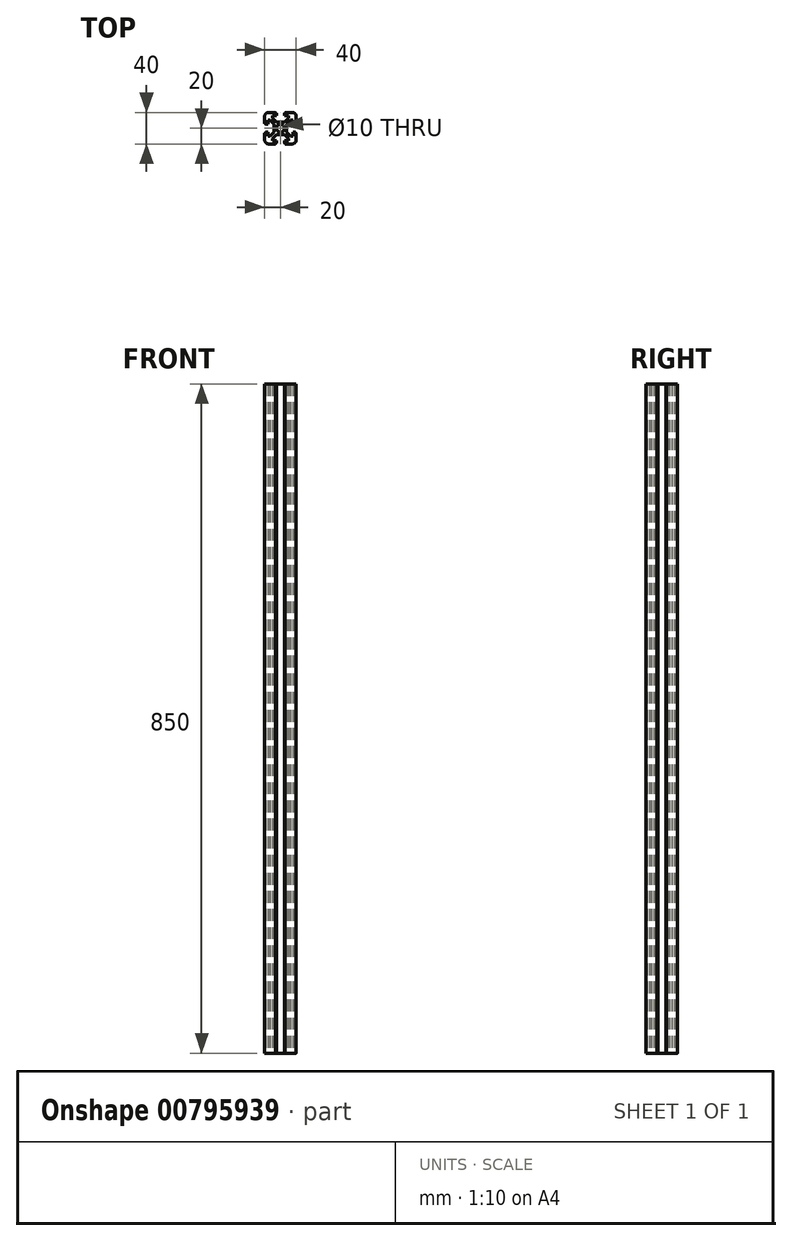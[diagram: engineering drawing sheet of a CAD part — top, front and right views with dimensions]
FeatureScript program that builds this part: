
annotation { "Feature Type Name" : "Feature", "Feature Type Description" : "" }
export const myFeature = defineFeature(function(context is Context, id is Id, definition is map)
    precondition{}
    {
        {
            var Q0;
            Q0=qCreatedBy(makeId("Top.planeOp"),FACE);
            var sketch = newSketch(context, id + "F0", { "sketchPlane" : qUnion([Q0])});
            skLineSegment(sketch, "E0", {"start": v(22.87, 22.87) * mm, "end": v(0, 0) * mm, "construction": true});
            skLineSegment(sketch, "E1", {"start": v(8, 0) * mm, "end": v(8, 5) * mm});
            skLineSegment(sketch, "E2", {"start": v(8, 5) * mm, "end": v(13, 10) * mm});
            skLineSegment(sketch, "E3", {"start": v(13, 10) * mm, "end": v(16, 10) * mm});
            skLineSegment(sketch, "E4", {"start": v(16, 10) * mm, "end": v(16, 5) * mm});
            skLineSegment(sketch, "E5", {"start": v(16, 5) * mm, "end": v(19, 5) * mm});
            skLineSegment(sketch, "E6", {"start": v(19, 5) * mm, "end": v(19, 6) * mm});
            skLineSegment(sketch, "E7", {"start": v(19, 6) * mm, "end": v(20, 6) * mm});
            skLineSegment(sketch, "E8", {"start": v(20, 6) * mm, "end": v(20, 15) * mm});
            skArc(sketch, "E9", {"start": v(20, 15) * mm, "mid": v(19.62, 16.91) * mm, "end": v(18.54, 18.54) * mm});
            skPoint(sketch, "E9.third.point", {"position": v(18.54, 18.54) * mm});
            skLineSegment(sketch, "E10.MirrorCS", {"start": v(6, 19) * mm, "end": v(6, 20) * mm});
            skLineSegment(sketch, "E11.MirrorCS", {"start": v(5, 19) * mm, "end": v(6, 19) * mm});
            skLineSegment(sketch, "E12.MirrorCS", {"start": v(6, 20) * mm, "end": v(15, 20) * mm});
            skLineSegment(sketch, "E13.MirrorCS", {"start": v(5, 16) * mm, "end": v(5, 19) * mm});
            skLineSegment(sketch, "E14.MirrorCS", {"start": v(10, 16) * mm, "end": v(5, 16) * mm});
            skLineSegment(sketch, "E15.MirrorCS", {"start": v(10, 13) * mm, "end": v(10, 16) * mm});
            skLineSegment(sketch, "E16.MirrorCS", {"start": v(5, 8) * mm, "end": v(10, 13) * mm});
            skLineSegment(sketch, "E17.MirrorCS", {"start": v(0, 8) * mm, "end": v(5, 8) * mm});
            skArc(sketch, "E18.MirrorCS", {"start": v(15, 20) * mm, "mid": v(16.91, 19.62) * mm, "end": v(18.54, 18.54) * mm});
            skLineSegment(sketch, "E19.1.0", {"start": v(-13, 10) * mm, "end": v(-16, 10) * mm});
            skLineSegment(sketch, "E19.1.1", {"start": v(-16, 10) * mm, "end": v(-16, 5) * mm});
            skLineSegment(sketch, "E19.1.2", {"start": v(-8, 5) * mm, "end": v(-13, 10) * mm});
            skPoint(sketch, "E19.1.3", {"position": v(-18.54, 18.54) * mm});
            skLineSegment(sketch, "E19.1.4", {"start": v(-8, 0) * mm, "end": v(-8, 5) * mm});
            skLineSegment(sketch, "E19.1.5", {"start": v(-16, 5) * mm, "end": v(-19, 5) * mm});
            skArc(sketch, "E19.1.6", {"start": v(-20, 15) * mm, "mid": v(-19.62, 16.91) * mm, "end": v(-18.54, 18.54) * mm});
            skLineSegment(sketch, "E19.1.7", {"start": v(-20, 6) * mm, "end": v(-20, 15) * mm});
            skArc(sketch, "E19.1.8", {"start": v(-15, 20) * mm, "mid": v(-16.91, 19.62) * mm, "end": v(-18.54, 18.54) * mm});
            skLineSegment(sketch, "E19.1.9", {"start": v(-6, 20) * mm, "end": v(-15, 20) * mm});
            skLineSegment(sketch, "E19.1.10", {"start": v(-5, 16) * mm, "end": v(-5, 19) * mm});
            skLineSegment(sketch, "E19.1.11", {"start": v(-10, 16) * mm, "end": v(-5, 16) * mm});
            skLineSegment(sketch, "E19.1.12", {"start": v(-5, 8) * mm, "end": v(-10, 13) * mm});
            skLineSegment(sketch, "E19.1.13", {"start": v(-10, 13) * mm, "end": v(-10, 16) * mm});
            skLineSegment(sketch, "E19.1.14", {"start": v(0, 8) * mm, "end": v(-5, 8) * mm});
            skPoint(sketch, "E19.1.15", {"position": v(-18.54, 18.54) * mm});
            skLineSegment(sketch, "E19.1.16", {"start": v(-19, 5) * mm, "end": v(-19, 6) * mm});
            skLineSegment(sketch, "E19.1.17", {"start": v(-19, 6) * mm, "end": v(-20, 6) * mm});
            skLineSegment(sketch, "E19.1.18", {"start": v(-6, 19) * mm, "end": v(-6, 20) * mm});
            skLineSegment(sketch, "E19.1.19", {"start": v(-5, 19) * mm, "end": v(-6, 19) * mm});
            skLineSegment(sketch, "E19.2.0", {"start": v(-10, -13) * mm, "end": v(-10, -16) * mm});
            skLineSegment(sketch, "E19.2.1", {"start": v(-10, -16) * mm, "end": v(-5, -16) * mm});
            skLineSegment(sketch, "E19.2.2", {"start": v(-5, -8) * mm, "end": v(-10, -13) * mm});
            skPoint(sketch, "E19.2.3", {"position": v(-18.54, -18.54) * mm});
            skLineSegment(sketch, "E19.2.4", {"start": v(0, -8) * mm, "end": v(-5, -8) * mm});
            skLineSegment(sketch, "E19.2.5", {"start": v(-5, -16) * mm, "end": v(-5, -19) * mm});
            skArc(sketch, "E19.2.6", {"start": v(-15, -20) * mm, "mid": v(-16.91, -19.62) * mm, "end": v(-18.54, -18.54) * mm});
            skLineSegment(sketch, "E19.2.7", {"start": v(-6, -20) * mm, "end": v(-15, -20) * mm});
            skArc(sketch, "E19.2.8", {"start": v(-20, -15) * mm, "mid": v(-19.62, -16.91) * mm, "end": v(-18.54, -18.54) * mm});
            skLineSegment(sketch, "E19.2.9", {"start": v(-20, -6) * mm, "end": v(-20, -15) * mm});
            skLineSegment(sketch, "E19.2.10", {"start": v(-16, -5) * mm, "end": v(-19, -5) * mm});
            skLineSegment(sketch, "E19.2.11", {"start": v(-16, -10) * mm, "end": v(-16, -5) * mm});
            skLineSegment(sketch, "E19.2.12", {"start": v(-8, -5) * mm, "end": v(-13, -10) * mm});
            skLineSegment(sketch, "E19.2.13", {"start": v(-13, -10) * mm, "end": v(-16, -10) * mm});
            skLineSegment(sketch, "E19.2.14", {"start": v(-8, 0) * mm, "end": v(-8, -5) * mm});
            skPoint(sketch, "E19.2.15", {"position": v(-18.54, -18.54) * mm});
            skLineSegment(sketch, "E19.2.16", {"start": v(-5, -19) * mm, "end": v(-6, -19) * mm});
            skLineSegment(sketch, "E19.2.17", {"start": v(-6, -19) * mm, "end": v(-6, -20) * mm});
            skLineSegment(sketch, "E19.2.18", {"start": v(-19, -6) * mm, "end": v(-20, -6) * mm});
            skLineSegment(sketch, "E19.2.19", {"start": v(-19, -5) * mm, "end": v(-19, -6) * mm});
            skLineSegment(sketch, "E19.3.0", {"start": v(13, -10) * mm, "end": v(16, -10) * mm});
            skLineSegment(sketch, "E19.3.1", {"start": v(16, -10) * mm, "end": v(16, -5) * mm});
            skLineSegment(sketch, "E19.3.2", {"start": v(8, -5) * mm, "end": v(13, -10) * mm});
            skPoint(sketch, "E19.3.3", {"position": v(18.54, -18.54) * mm});
            skLineSegment(sketch, "E19.3.4", {"start": v(8, 0) * mm, "end": v(8, -5) * mm});
            skLineSegment(sketch, "E19.3.5", {"start": v(16, -5) * mm, "end": v(19, -5) * mm});
            skArc(sketch, "E19.3.6", {"start": v(20, -15) * mm, "mid": v(19.62, -16.91) * mm, "end": v(18.54, -18.54) * mm});
            skLineSegment(sketch, "E19.3.7", {"start": v(20, -6) * mm, "end": v(20, -15) * mm});
            skArc(sketch, "E19.3.8", {"start": v(15, -20) * mm, "mid": v(16.91, -19.62) * mm, "end": v(18.54, -18.54) * mm});
            skLineSegment(sketch, "E19.3.9", {"start": v(6, -20) * mm, "end": v(15, -20) * mm});
            skLineSegment(sketch, "E19.3.10", {"start": v(5, -16) * mm, "end": v(5, -19) * mm});
            skLineSegment(sketch, "E19.3.11", {"start": v(10, -16) * mm, "end": v(5, -16) * mm});
            skLineSegment(sketch, "E19.3.12", {"start": v(5, -8) * mm, "end": v(10, -13) * mm});
            skLineSegment(sketch, "E19.3.13", {"start": v(10, -13) * mm, "end": v(10, -16) * mm});
            skLineSegment(sketch, "E19.3.14", {"start": v(0, -8) * mm, "end": v(5, -8) * mm});
            skPoint(sketch, "E19.3.15", {"position": v(18.54, -18.54) * mm});
            skLineSegment(sketch, "E19.3.16", {"start": v(19, -5) * mm, "end": v(19, -6) * mm});
            skLineSegment(sketch, "E19.3.17", {"start": v(19, -6) * mm, "end": v(20, -6) * mm});
            skLineSegment(sketch, "E19.3.18", {"start": v(6, -19) * mm, "end": v(6, -20) * mm});
            skLineSegment(sketch, "E19.3.19", {"start": v(5, -19) * mm, "end": v(6, -19) * mm});
            skPoint(sketch, "E19.center", {"position": v(0, 0) * mm});
            skSolve(sketch);
        }
        {
            var Q0;
            Q0 = qSketchRegion(id + "F0", true);
            extrude(context, id + "F1", {"entities" : qUnion([Q0]), "depth" : 850 * mm, "offsetDistance" : 25 * mm});
        }
        {
            var Q0;
            Q0=makeQuery(id+"F1.opExtrude","CAP_FACE",FACE,{"disambiguationData":[OSD([sQuery(id+"F0.wireOp",EDGE,"E1"),sQuery(id+"F0.wireOp",EDGE,"E2"),sQuery(id+"F0.wireOp",EDGE,"E3"),sQuery(id+"F0.wireOp",EDGE,"E4"),sQuery(id+"F0.wireOp",EDGE,"E5"),sQuery(id+"F0.wireOp",EDGE,"E6"),sQuery(id+"F0.wireOp",EDGE,"E7"),sQuery(id+"F0.wireOp",EDGE,"E8"),sQuery(id+"F0.wireOp",EDGE,"E9"),sQuery(id+"F0.wireOp",EDGE,"E10.MirrorCS"),sQuery(id+"F0.wireOp",EDGE,"E11.MirrorCS"),sQuery(id+"F0.wireOp",EDGE,"E12.MirrorCS"),sQuery(id+"F0.wireOp",EDGE,"E13.MirrorCS"),sQuery(id+"F0.wireOp",EDGE,"E14.MirrorCS"),sQuery(id+"F0.wireOp",EDGE,"E15.MirrorCS"),sQuery(id+"F0.wireOp",EDGE,"E16.MirrorCS"),sQuery(id+"F0.wireOp",EDGE,"E17.MirrorCS"),sQuery(id+"F0.wireOp",EDGE,"E18.MirrorCS"),sQuery(id+"F0.wireOp",EDGE,"E19.1.0"),sQuery(id+"F0.wireOp",EDGE,"E19.1.1"),sQuery(id+"F0.wireOp",EDGE,"E19.1.2"),sQuery(id+"F0.wireOp",EDGE,"E19.1.4"),sQuery(id+"F0.wireOp",EDGE,"E19.1.5"),sQuery(id+"F0.wireOp",EDGE,"E19.1.6"),sQuery(id+"F0.wireOp",EDGE,"E19.1.7"),sQuery(id+"F0.wireOp",EDGE,"E19.1.8"),sQuery(id+"F0.wireOp",EDGE,"E19.1.9"),sQuery(id+"F0.wireOp",EDGE,"E19.1.10"),sQuery(id+"F0.wireOp",EDGE,"E19.1.11"),sQuery(id+"F0.wireOp",EDGE,"E19.1.12"),sQuery(id+"F0.wireOp",EDGE,"E19.1.13"),sQuery(id+"F0.wireOp",EDGE,"E19.1.14"),sQuery(id+"F0.wireOp",EDGE,"E19.1.16"),sQuery(id+"F0.wireOp",EDGE,"E19.1.17"),sQuery(id+"F0.wireOp",EDGE,"E19.1.18"),sQuery(id+"F0.wireOp",EDGE,"E19.1.19"),sQuery(id+"F0.wireOp",EDGE,"E19.2.0"),sQuery(id+"F0.wireOp",EDGE,"E19.2.1"),sQuery(id+"F0.wireOp",EDGE,"E19.2.2"),sQuery(id+"F0.wireOp",EDGE,"E19.2.4"),sQuery(id+"F0.wireOp",EDGE,"E19.2.5"),sQuery(id+"F0.wireOp",EDGE,"E19.2.6"),sQuery(id+"F0.wireOp",EDGE,"E19.2.7"),sQuery(id+"F0.wireOp",EDGE,"E19.2.8"),sQuery(id+"F0.wireOp",EDGE,"E19.2.9"),sQuery(id+"F0.wireOp",EDGE,"E19.2.10"),sQuery(id+"F0.wireOp",EDGE,"E19.2.11"),sQuery(id+"F0.wireOp",EDGE,"E19.2.12"),sQuery(id+"F0.wireOp",EDGE,"E19.2.13"),sQuery(id+"F0.wireOp",EDGE,"E19.2.14"),sQuery(id+"F0.wireOp",EDGE,"E19.2.16"),sQuery(id+"F0.wireOp",EDGE,"E19.2.17"),sQuery(id+"F0.wireOp",EDGE,"E19.2.18"),sQuery(id+"F0.wireOp",EDGE,"E19.2.19"),sQuery(id+"F0.wireOp",EDGE,"E19.3.0"),sQuery(id+"F0.wireOp",EDGE,"E19.3.1"),sQuery(id+"F0.wireOp",EDGE,"E19.3.2"),sQuery(id+"F0.wireOp",EDGE,"E19.3.4"),sQuery(id+"F0.wireOp",EDGE,"E19.3.5"),sQuery(id+"F0.wireOp",EDGE,"E19.3.6"),sQuery(id+"F0.wireOp",EDGE,"E19.3.7"),sQuery(id+"F0.wireOp",EDGE,"E19.3.8"),sQuery(id+"F0.wireOp",EDGE,"E19.3.9"),sQuery(id+"F0.wireOp",EDGE,"E19.3.10"),sQuery(id+"F0.wireOp",EDGE,"E19.3.11"),sQuery(id+"F0.wireOp",EDGE,"E19.3.12"),sQuery(id+"F0.wireOp",EDGE,"E19.3.13"),sQuery(id+"F0.wireOp",EDGE,"E19.3.14"),sQuery(id+"F0.wireOp",EDGE,"E19.3.16"),sQuery(id+"F0.wireOp",EDGE,"E19.3.17"),sQuery(id+"F0.wireOp",EDGE,"E19.3.18"),sQuery(id+"F0.wireOp",EDGE,"E19.3.19")])],"isStart":false});
            var sketch = newSketch(context, id + "F2", { "sketchPlane" : qUnion([Q0])});
            skCircle(sketch, "E20", {"center": v(0, 0) * mm, "radius": 5 * mm});
            skSolve(sketch);
        }
        {
            var Q0;
            Q0 = qSketchRegion(id + "F2", true);
            extrude(context, id + "F3", {"entities" : qUnion([Q0]), "operationType" : NewBodyOperationType.REMOVE, "endBound" : BoundingType.UP_TO_NEXT, "oppositeDirection" : true, "depth" : 50 * mm, "offsetDistance" : 25 * mm});
        }
    });
